FCSTD DOCUMENT  (FreeCAD 0.17R10279 (Git))
Label: truss
License: All rights reserved
LicenseURL: http://en.wikipedia.org/wiki/All_rights_reserved
objects: Sketcher::SketchObject×1
note: 1 computed .brp shape members not serialized (recipe doc carries the construction recipe); baked Part::Feature solids carry a one-line shape summary decoded from their .brp

FEATURE [Sketcher::SketchObject] Sketch
  sketch-geometry (7):
    g0: LineSegment StartX=1000 StartY=0 StartZ=0 EndX=2000 EndY=0 EndZ=0
    g1: LineSegment StartX=2000 StartY=0 StartZ=0 EndX=1500 EndY=866.025 EndZ=0
    g2: LineSegment StartX=1500 StartY=866.025 StartZ=0 EndX=500 EndY=866.025 EndZ=0
    g3: LineSegment StartX=500 StartY=866.025 StartZ=0 EndX=0 EndY=0 EndZ=0
    g4: LineSegment StartX=500 StartY=866.025 StartZ=0 EndX=1000 EndY=0 EndZ=0
    g5: LineSegment StartX=1000 StartY=0 StartZ=0 EndX=1500 EndY=866.025 EndZ=0
    g6: LineSegment StartX=0 StartY=0 StartZ=0 EndX=1000 EndY=0 EndZ=0
  constraints (18):
    c: Coincident(g0,g1)
    c: Coincident(g1,g2)
    c: Coincident(g2,g3)
    c: Horizontal(g0)
    c: Horizontal(g2)
    c: Coincident(g3,g-1)
    c: DistanceX(g2,g2) = 1000
    c: Coincident(g4,g2)
    c: Coincident(g5,g1)
    c: Coincident(g0,g5)
    c: Coincident(g6,g-1)
    c: Coincident(g6,g0)
    c: Horizontal(g6)
    c: Coincident(g4,g0)
    c: Equal(g6,g2)
    c: Equal(g0,g2)
    c: Equal(g3,g1)
    c: Equal(g3,g2)
